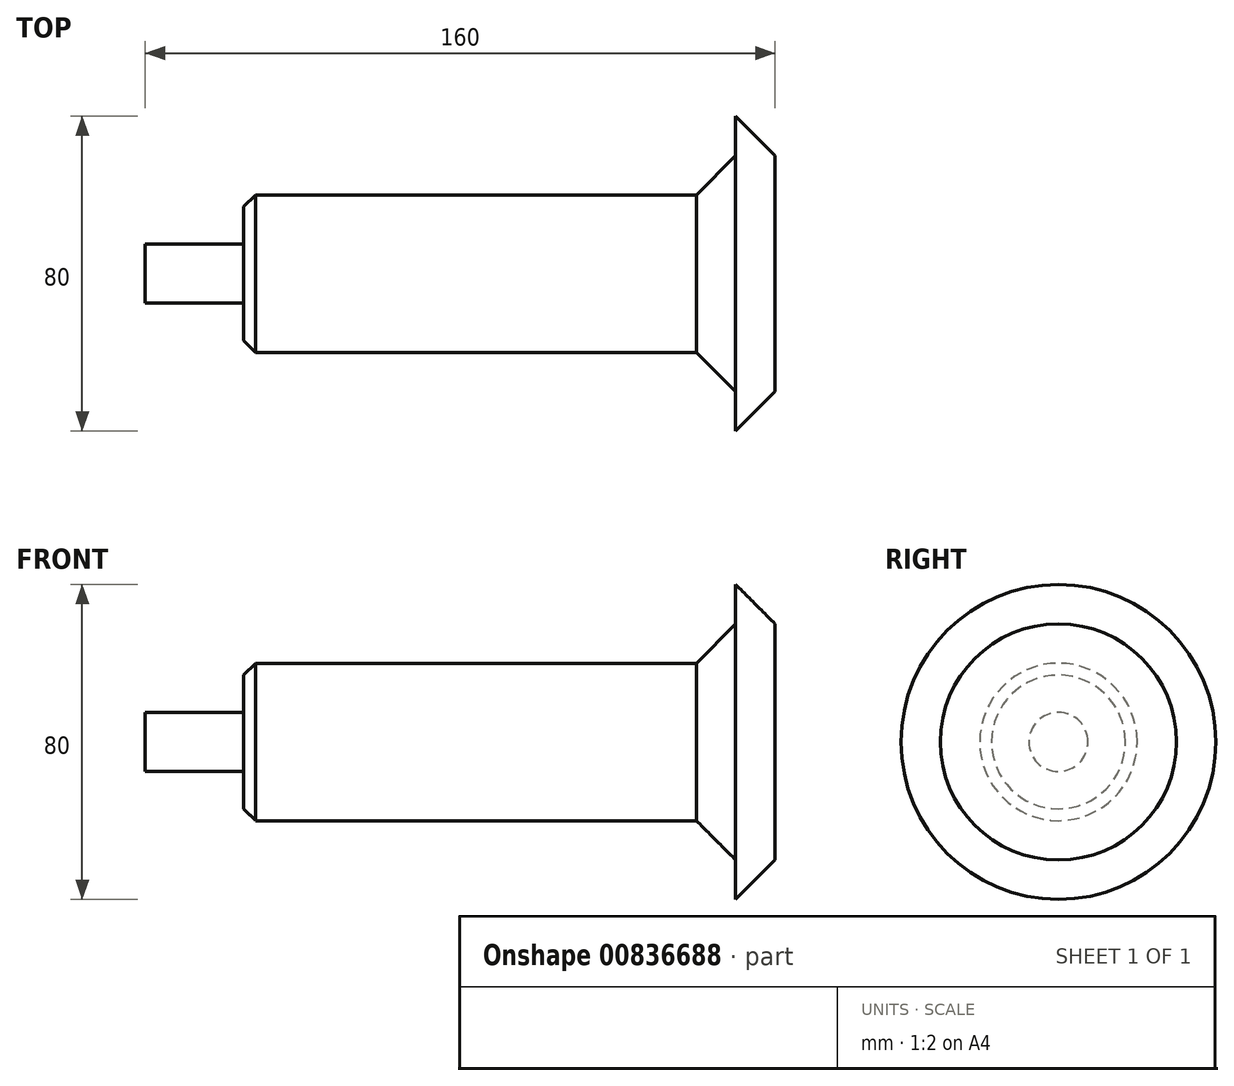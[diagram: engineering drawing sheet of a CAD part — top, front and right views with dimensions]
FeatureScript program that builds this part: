
annotation { "Feature Type Name" : "Feature", "Feature Type Description" : "" }
export const myFeature = defineFeature(function(context is Context, id is Id, definition is map)
    precondition{}
    {
        {
            var Q0;
            Q0=qCreatedBy(makeId("Top.planeOp"),FACE);
            var sketch = newSketch(context, id + "F0", { "sketchPlane" : qUnion([Q0])});
            skLineSegment(sketch, "E0", {"start": v(-80, 0) * mm, "end": v(-80, 7.5) * mm});
            skLineSegment(sketch, "E1", {"start": v(-80, 7.5) * mm, "end": v(-55, 7.5) * mm});
            skLineSegment(sketch, "E2", {"start": v(-55, 7.5) * mm, "end": v(-55, 20) * mm});
            skLineSegment(sketch, "E3", {"start": v(-55, 20) * mm, "end": v(70, 20) * mm});
            skLineSegment(sketch, "E4", {"start": v(70, 20) * mm, "end": v(70, 40) * mm});
            skLineSegment(sketch, "E5", {"start": v(70, 40) * mm, "end": v(80, 40) * mm});
            skLineSegment(sketch, "E6", {"start": v(80, 40) * mm, "end": v(80, 0) * mm});
            skLineSegment(sketch, "E7", {"start": v(80, 0) * mm, "end": v(-80, 0) * mm});
            skSolve(sketch);
        }
        {
            var Q0;
            Q0 = qSketchRegion(id + "F0", true);
            var Q1;
            Q1=sQuery(id+"F0.wireOp",EDGE,"E7");
            revolve(context, id + "F1", {"surfaceOperationType" : NewSurfaceOperationType.NEW, "entities" : qUnion([Q0]), "axis" : qUnion([Q1]), "revolveType" : RevolveType.FULL});
        }
        {
            var Q0;
            Q0=makeQuery(id+"F1.opRevolve","SWEPT_EDGE",EDGE,{"disambiguationData":[OSD([sQuery(id+"F0.wireOp",EDGE,"E3"),sQuery(id+"F0.wireOp",EDGE,"E4")])]});
            chamfer(context, id + "F2", {"entities" : qUnion([Q0]), "chamferType" : ChamferType.OFFSET_ANGLE, "width" : 10 * mm, "oppositeDirection" : false, "angle" : 45 * degree, "tangentPropagation" : true});
        }
        {
            var Q0;
            Q0=makeQuery(id+"F1.opRevolve","SWEPT_EDGE",EDGE,{"disambiguationData":[OSD([sQuery(id+"F0.wireOp",EDGE,"E5"),sQuery(id+"F0.wireOp",EDGE,"E6")])]});
            chamfer(context, id + "F3", {"entities" : qUnion([Q0]), "chamferType" : ChamferType.OFFSET_ANGLE, "width" : 10 * mm, "oppositeDirection" : false, "angle" : 45 * degree, "tangentPropagation" : true});
        }
        {
            var Q0;
            Q0=makeQuery(id+"F1.opRevolve","SWEPT_EDGE",EDGE,{"disambiguationData":[OSD([sQuery(id+"F0.wireOp",EDGE,"E2"),sQuery(id+"F0.wireOp",EDGE,"E3")])]});
            chamfer(context, id + "F4", {"entities" : qUnion([Q0]), "chamferType" : ChamferType.OFFSET_ANGLE, "width" : 3 * mm, "oppositeDirection" : false, "angle" : 45 * degree, "tangentPropagation" : true});
        }
    });
